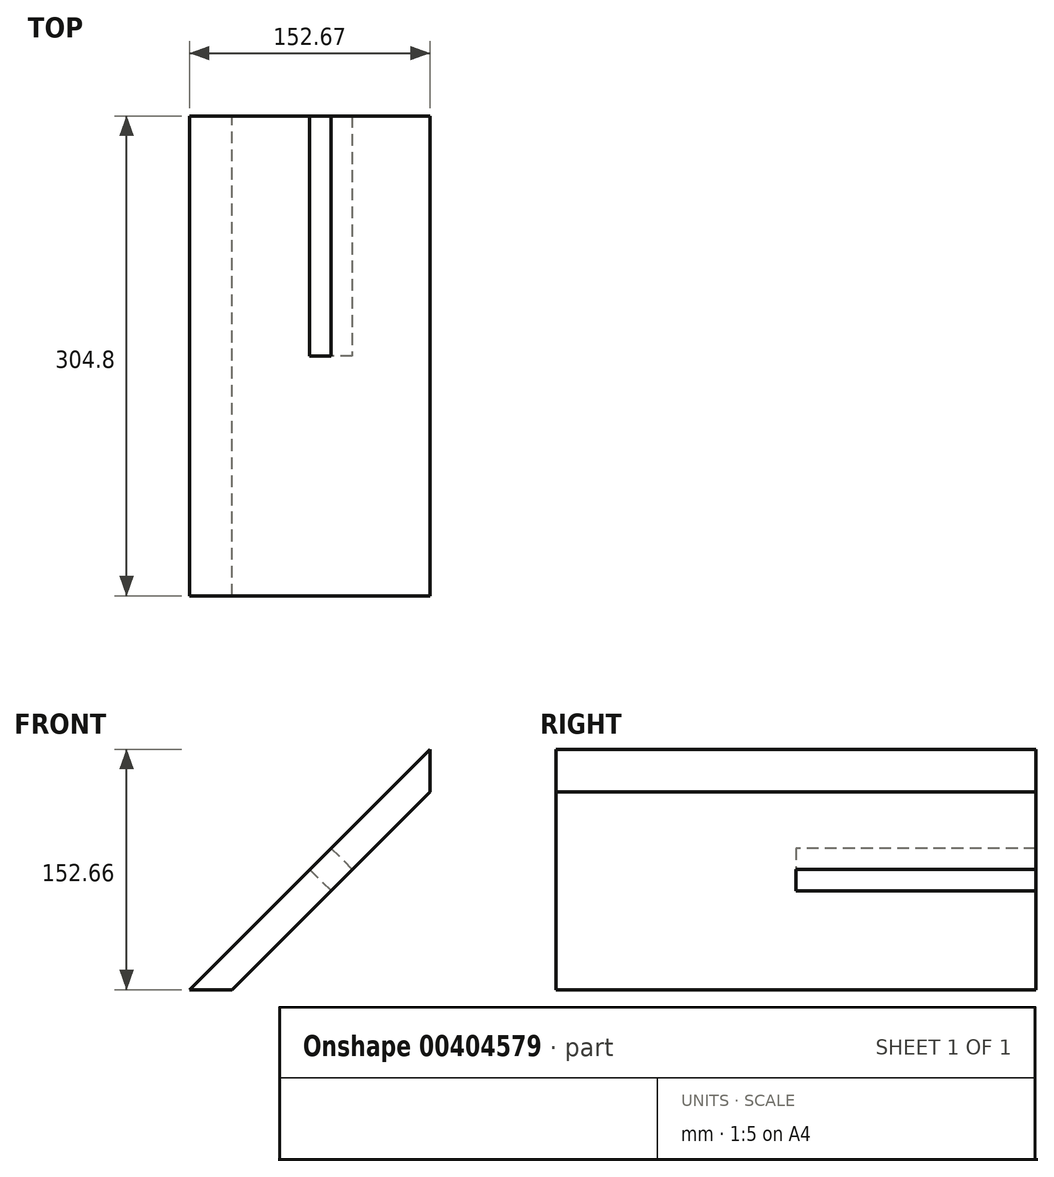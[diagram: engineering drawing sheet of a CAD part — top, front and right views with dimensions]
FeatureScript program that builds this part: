
annotation { "Feature Type Name" : "Feature", "Feature Type Description" : "" }
export const myFeature = defineFeature(function(context is Context, id is Id, definition is map)
    precondition{}
    {
        {
            var Q0;
            Q0=qCreatedBy(makeId("Front.planeOp"),FACE);
            var sketch = newSketch(context, id + "F0", { "sketchPlane" : qUnion([Q0])});
            skLineSegment(sketch, "E0", {"start": v(-337.22, 0) * mm, "end": v(-184.55, 152.66) * mm});
            skPoint(sketch, "E1.MirrorP", {"position": v(53.93, 355.6) * mm});
            skLineSegment(sketch, "E2.MirrorCS", {"start": v(-310.28, 0) * mm, "end": v(-184.55, 125.72) * mm});
            skLineSegment(sketch, "E3", {"start": v(-310.28, 0) * mm, "end": v(-337.22, 0) * mm});
            skLineSegment(sketch, "E4", {"start": v(-184.55, 152.66) * mm, "end": v(-184.55, 125.72) * mm});
            skSolve(sketch);
        }
        {
            var Q0;
            Q0=qSketchRegion(id+"F0",true);
            extrude(context, id + "F1", {"entities" : qUnion([Q0]), "endBound" : BoundingType.SYMMETRIC, "depth" : 304.8 * mm});
        }
        {
            var Q0;
            Q0=makeQuery(id+"F1.opExtrude","SWEPT_FACE",FACE,{"disambiguationData":[OSD([sQuery(id+"F0.wireOp",EDGE,"E2.MirrorCS")])]});
            var sketch = newSketch(context, id + "F2", { "sketchPlane" : qUnion([Q0])});
            skLineSegment(sketch, "E5.bottom", {"start": v(152.4, -111.45) * mm, "end": v(0, -111.45) * mm});
            skLineSegment(sketch, "E5.top", {"start": v(152.4, -130.5) * mm, "end": v(0, -130.5) * mm});
            skLineSegment(sketch, "E5.left", {"start": v(152.4, -111.45) * mm, "end": v(152.4, -130.5) * mm});
            skLineSegment(sketch, "E5.right", {"start": v(0, -111.45) * mm, "end": v(0, -130.5) * mm});
            skSolve(sketch);
        }
        {
            var Q0;
            Q0=qSketchRegion(id+"F2",true);
            extrude(context, id + "F3", {"entities" : qUnion([Q0]), "operationType" : NewBodyOperationType.REMOVE, "oppositeDirection" : true, "depth" : 19.05 * mm});
        }
    });
